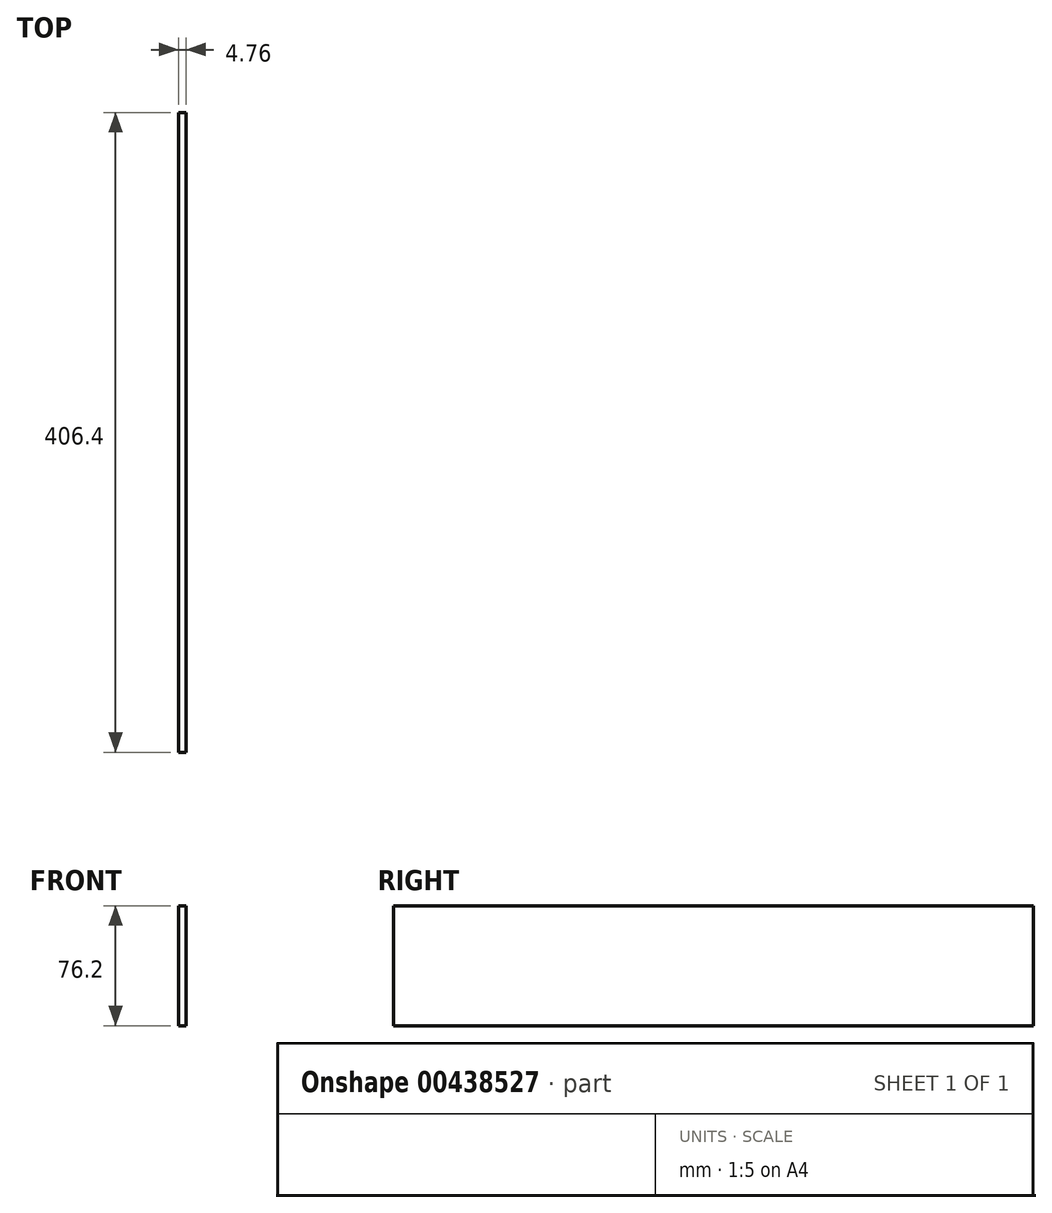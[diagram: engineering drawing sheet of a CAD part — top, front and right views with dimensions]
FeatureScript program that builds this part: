
annotation { "Feature Type Name" : "Feature", "Feature Type Description" : "" }
export const myFeature = defineFeature(function(context is Context, id is Id, definition is map)
    precondition{}
    {
        {
            var Q0;
            Q0=qCreatedBy(makeId("Right.planeOp"),FACE);
            var sketch = newSketch(context, id + "F0", { "sketchPlane" : qUnion([Q0])});
            skLineSegment(sketch, "E0.bottom", {"start": v(-176.88, -53.61) * mm, "end": v(229.52, -53.61) * mm});
            skLineSegment(sketch, "E0.top", {"start": v(-176.88, -129.81) * mm, "end": v(229.52, -129.81) * mm});
            skLineSegment(sketch, "E0.left", {"start": v(-176.88, -53.61) * mm, "end": v(-176.88, -129.81) * mm});
            skLineSegment(sketch, "E0.right", {"start": v(229.52, -53.61) * mm, "end": v(229.52, -129.81) * mm});
            skSolve(sketch);
        }
        {
            var Q0;
            Q0=makeQuery(id+"F0.imprint","IMPRINT",FACE,{"disambiguationData":[TD([[makeQuery(id+"F0.imprint","IMPRINT",EDGE,{"derivedFrom":sQuery(id+"F0.wireOp",EDGE,"E0.bottom")}),-1.0]])]});
            extrude(context, id + "F1", {"entities" : qUnion([Q0]), "depth" : 4.76 * mm});
        }
    });
